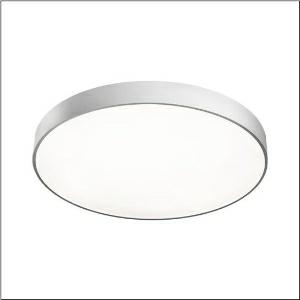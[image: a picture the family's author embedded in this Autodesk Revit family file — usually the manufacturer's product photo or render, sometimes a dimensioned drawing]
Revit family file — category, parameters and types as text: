
# Revit family: round_21_l_51mr38fd0421s
name_source: partatom
category: Lighting Fixtures
units: mm (PartAtom-declared; Revit-internal decimal feet)

## family parameters
Cut with Voids When Loaded = No
Host = Face
Light Source = No
Part Type = Normal
Room Calculation Point = No
Round Connector Dimension = Use Diameter
Shared = No

## types (1)
- Round 21 L (1 x LED, 14150 lm, 97 W, 4000K)
    Apparent Load = 97 VA
    CIE Flux Codes = 49 80 96 100 100
    Color Rendering = 80
    Color Temperature = 4000K
    Default Elevation = 1800 mm
    Description = Round 21 L, wall and ceiling luminaire, primary optical cover: cover, of PMMA, opal, light emission: direct distribution, primary light characteristic: symmetric, installation type: suspended mounting, surface-mounted, LED, rated luminous flux: 13.080lm, luminous efficacy: 146lm/W, light colour: 840, colour temperature: 4000K, control gear: DALI 2, with terminal, 5-pole, mains connection: 230V, AC, 50/60Hz, rated input power: 97W, housing, of aluminium, coated, silver, diameter: 850mm, height: 62mm, protection rating (complete): IP40, insulation class (complete): insulation class I (protective earthing), certification: CE, impact resistance: IK04, permissible operating ambient temperature: -10..+35°C, packaging unit: 1 piece
    Height = 87 mm
    Lamp = 1 x LED
    Lamp Light Flux = 14150 lm
    Lamp Power = 97 W
    Lamp count = 1
    Length = 850 mm
    Luminous efficacy = 146 lm/W
    Manufacturer = Siteco
    ModVariant = No
    Model = 51MR38FD0421S
    Mounting Place = Ceiling
    Mounting Type = Surface mounted
    Number of Poles = 1
    OnlyDefault = Yes
    Power Factor = 1
    Product Name = Round 21 L
    Product group = wall and ceiling luminaire
    ProductGroupID = 304
    Protection Class = Protection class I
    Protection Degree = IP 40
    RLX_Detail_Level = 1
    RLX_Emergency_Light_Flux = 0 lm
    RLX_Emergency_Type = 0
    RLX_Emergency_Type_DB = No
    RlxData = <blob elided: 20237 chars, md5=b460428e>
    Socket = socket
    Standby Power = 0 W
    System Light Flux = 14150 lm
    System Power = 97 W
    Type Comments = Product without accessories
    Type Image = l_1258324.jpg
    URL = http://relux.com
    VarID = ---
    Voltage = 0 V
    Weight = 0.00 kg
    Width = 0 mm  [stored 0 ft]

note: [stored X ft] marks values corroborated as IEEE doubles in the binary element streams (Revit-internal decimal feet)

## geometry (parser evidence)
native form markers: Blend x4, Sweep x12
no freeform markers — native parametric forms only
